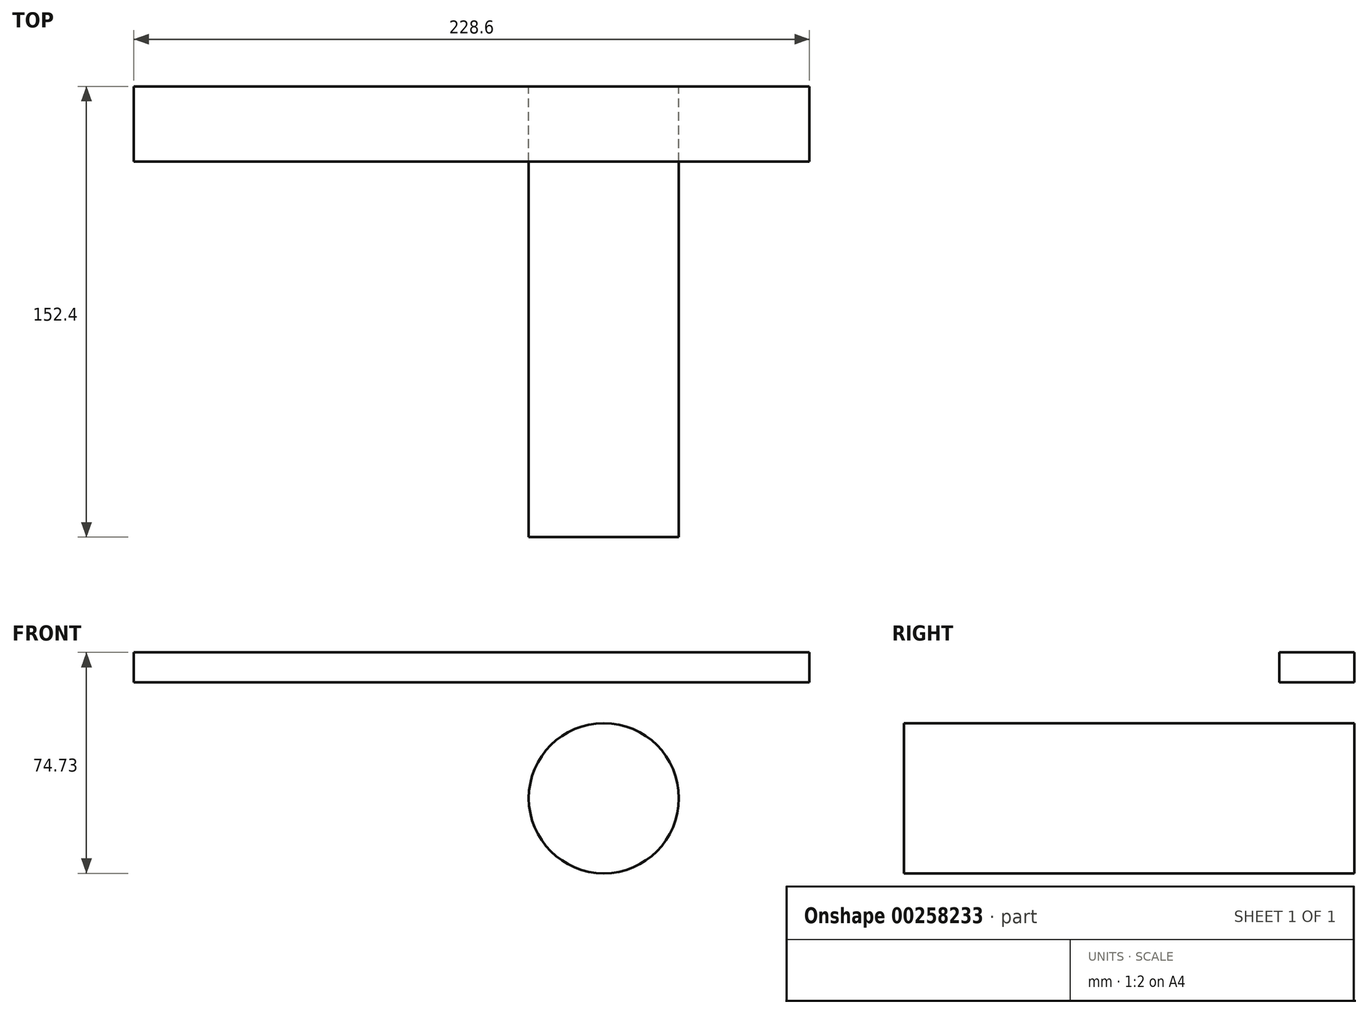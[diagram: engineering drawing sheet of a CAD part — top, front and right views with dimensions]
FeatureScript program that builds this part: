
annotation { "Feature Type Name" : "Feature", "Feature Type Description" : "" }
export const myFeature = defineFeature(function(context is Context, id is Id, definition is map)
    precondition{}
    {
        {
            var Q0;
            Q0=qCreatedBy(makeId("Front.planeOp"),FACE);
            var sketch = newSketch(context, id + "F0", { "sketchPlane" : qUnion([Q0])});
            skCircle(sketch, "E0", {"center": v(0, 0) * mm, "radius": 25.4 * mm});
            skSolve(sketch);
        }
        {
            var Q0;
            Q0=makeQuery(id+"F0.imprint","IMPRINT",FACE,{"disambiguationData":[TD([[makeQuery(id+"F0.imprint","IMPRINT",EDGE,{"derivedFrom":sQuery(id+"F0.wireOp",EDGE,"E0")}),1.0]])]});
            extrude(context, id + "F1", {"entities" : qUnion([Q0]), "depth" : 152.4 * mm});
        }
        {
            var Q0;
            Q0=qCreatedBy(makeId("Front.planeOp"),FACE);
            var sketch = newSketch(context, id + "F2", { "sketchPlane" : qUnion([Q0])});
            skLineSegment(sketch, "E1.bottom", {"start": v(69.57, 49.33) * mm, "end": v(-159.03, 49.33) * mm});
            skLineSegment(sketch, "E1.top", {"start": v(69.57, 39.17) * mm, "end": v(-159.03, 39.17) * mm});
            skLineSegment(sketch, "E1.left", {"start": v(69.57, 49.33) * mm, "end": v(69.57, 39.17) * mm});
            skLineSegment(sketch, "E1.right", {"start": v(-159.03, 49.33) * mm, "end": v(-159.03, 39.17) * mm});
            skPoint(sketch, "E1.middle", {"position": v(-44.73, 44.25) * mm});
            skSolve(sketch);
        }
        {
            var Q0;
            Q0=makeQuery(id+"F2.imprint","IMPRINT",FACE,{"disambiguationData":[TD([[makeQuery(id+"F2.imprint","IMPRINT",EDGE,{"derivedFrom":sQuery(id+"F2.wireOp",EDGE,"E1.bottom")}),1.0]])]});
            extrude(context, id + "F3", {"entities" : qUnion([Q0]), "depth" : 25.4 * mm});
        }
    });
